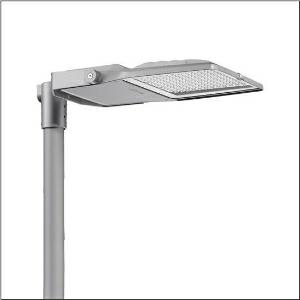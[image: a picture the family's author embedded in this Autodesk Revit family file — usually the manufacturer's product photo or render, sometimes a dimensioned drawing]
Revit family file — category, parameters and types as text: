
# Revit family: floodlight_fl_21_midi___pl52_5xa7786e4d3a_a426
name_source: partatom
category: Lighting Fixtures
units: mm (PartAtom-declared; Revit-internal decimal feet)

## family parameters
Cut with Voids When Loaded = No
Host = Face
Light Source = No
Part Type = Normal
Room Calculation Point = No
Round Connector Dimension = Use Diameter
Shared = No

## types (1)
- --- (1 x LED, 28110 lm, 212.4 W, 4000K)
    Apparent Load = 212 VA
    CIE Flux Codes = 26 60 98 100 100
    Color Rendering = 70
    Color Temperature = 4000K
    Default Elevation = 1800 mm
    Description = Floodlight FL 21 midi, floodlight, primary light control with lens, of PMMA, primary optical cover: protective disc, of toughened safety glass, transparent, light distribution: PL52, light emission: direct distribution, installation type: surface-mounted, LED, High Power LED, rated luminous flux: 28.110lm, luminous efficacy: 132lm/W, light colour: 740, colour temperature: 4000K, control gear: Smart Interface (Zhaga)D4i, control: overheat protection, constant luminous flux control, time-dependent luminous flux control, flexible luminous flux parameterisation, pre-setting: logarithmic dimming characteristic, with terminal, 6-pole, mains connection: 220..240V, AC, 50/60Hz, start of lifetime: 212W, end of service life: 231W, reduction: 95W, mast bracket, of diecast aluminium, powder-coated, Siteco® metallic grey (DB 702S), corrosivity category C5 mid according to DIN EN ISO 12944, suitable for swimming pools, chlorine-resistant, sealing non-destructively replaceable, mast bracket, of steel, galvanised, powder-coated, Siteco® metallic grey (DB 702S), Smart Interface below and above, protection rating (complete): IP66, insulation class (complete): insulation class II (safety insulation), certification: CE, ENEC, VDE, protection symbol: D, impact resistance: IK08, permissible operating ambient temperature: -40..+40°C, permissible operating ambient temperature for outdoor applications: -40..+50°C, standard: DIN EN 12944, LABS conformity tested according to VDMA 24364:2018-05, packaging unit: 1 piece

Light Distribution: PL52
    Height = 76 mm
    Lamp = 1 x LED
    Lamp Light Flux = 28110 lm
    Lamp Power = 212.4 W
    Lamp count = 1
    Length = 657 mm
    Luminous efficacy = 132 lm/W
    Manufacturer = Siteco
    ModVariant = No
    Model = 5XA7786E4D3A
    Number of Poles = 1
    OnlyDefault = Yes
    Power Factor = 1
    Product Name = Floodlight FL 21 midi | PL52
    Product group = floodlight | pylon annexe
    ProductGroupID = 6201
    Protection Class = Protection class II
    Protection Degree = IP 66
    RLX_Detail_Level = 1
    RLX_Emergency_Light_Flux = 0 lm
    RLX_Emergency_Type = 0
    RLX_Emergency_Type_DB = No
    RlxData = <blob elided: 104745 chars, md5=0e7407e8>
    Socket = socket
    Standby Power = 0 W
    System Light Flux = 28110 lm
    System Power = 212 W
    Type Comments = factory setting: luminous flux: 100 % | dim-lin: 254 | 710 mA
    Type Image = l_1007123.jpg
    URL = http://relux.com
    VarID = @adj_110811
    Voltage = 0 V
    Weight = 0.00 kg
    Width = 442 mm

## geometry (parser evidence)
native form markers: Blend x4, Sweep x12
no freeform markers — native parametric forms only
